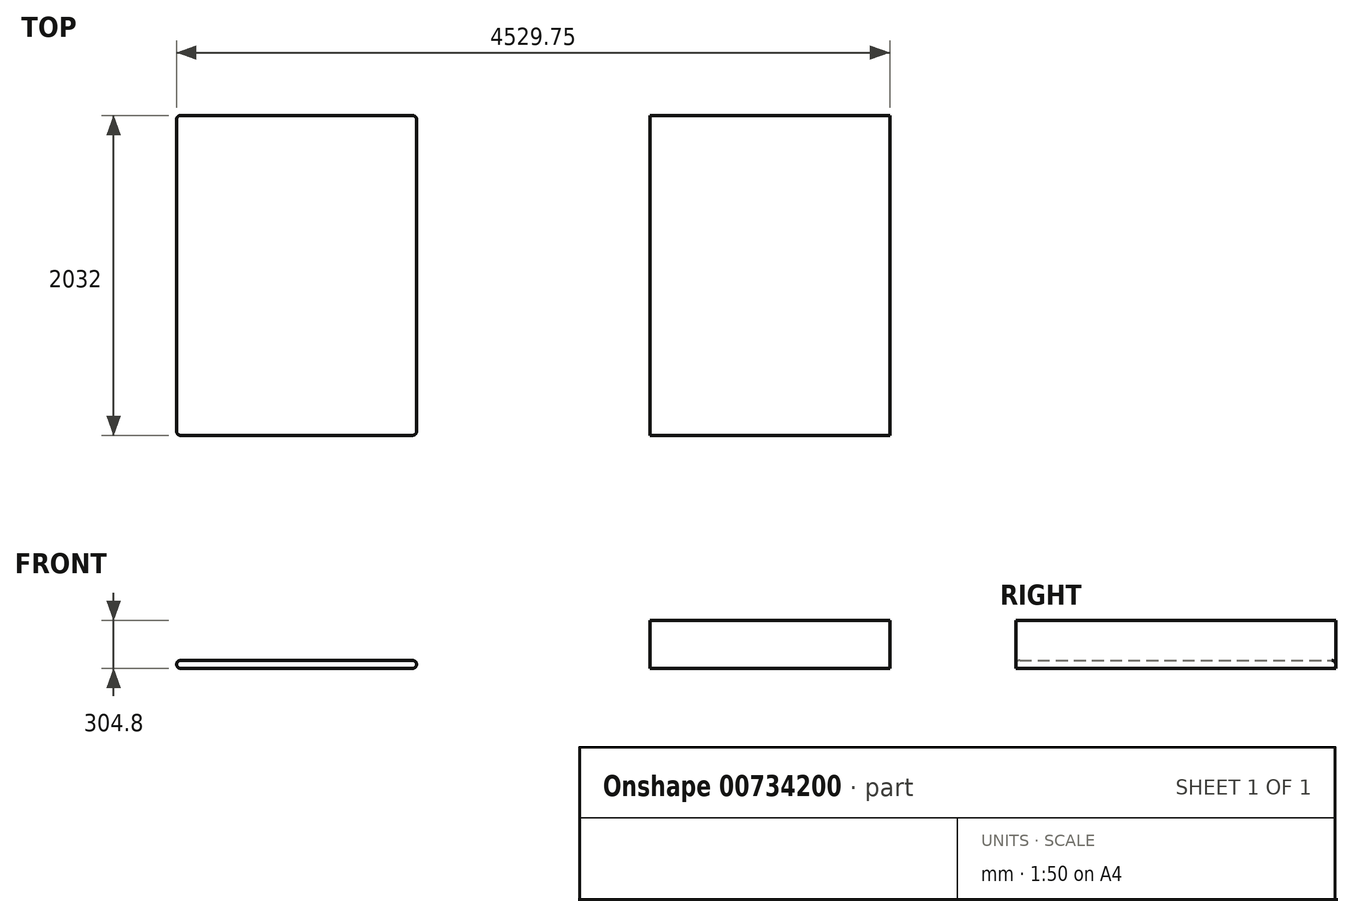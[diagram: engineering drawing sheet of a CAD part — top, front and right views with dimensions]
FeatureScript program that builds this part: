
annotation { "Feature Type Name" : "Feature", "Feature Type Description" : "" }
export const myFeature = defineFeature(function(context is Context, id is Id, definition is map)
    precondition{}
    {
        {
            var Q0;
            Q0=qCreatedBy(makeId("Top.planeOp"),FACE);
            var sketch = newSketch(context, id + "F0", { "sketchPlane" : qUnion([Q0])});
            skLineSegment(sketch, "E0.bottom", {"start": v(762, -1016) * mm, "end": v(-762, -1016) * mm});
            skLineSegment(sketch, "E0.top", {"start": v(762, 1016) * mm, "end": v(-762, 1016) * mm});
            skLineSegment(sketch, "E0.left", {"start": v(762, -1016) * mm, "end": v(762, 1016) * mm});
            skLineSegment(sketch, "E0.right", {"start": v(-762, -1016) * mm, "end": v(-762, 1016) * mm});
            skPoint(sketch, "E0.middle", {"position": v(0, 0) * mm});
            skSolve(sketch);
        }
        {
            var Q0;
            Q0=makeQuery(id+"F0.imprint","IMPRINT",FACE,{"disambiguationData":[TD([[makeQuery(id+"F0.imprint","IMPRINT",EDGE,{"derivedFrom":sQuery(id+"F0.wireOp",EDGE,"E0.bottom")}),-1.0]])]});
            extrude(context, id + "F1", {"entities" : qUnion([Q0]), "depth" : 304.8 * mm, "offsetDistance" : 25.4 * mm});
        }
        {
            var Q0;
            Q0=qCreatedBy(makeId("Top.planeOp"),FACE);
            var sketch = newSketch(context, id + "F2", { "sketchPlane" : qUnion([Q0])});
            skLineSegment(sketch, "E1.bottom", {"start": v(-2243.75, -1016) * mm, "end": v(-3767.75, -1016) * mm});
            skLineSegment(sketch, "E1.top", {"start": v(-2243.75, 1016) * mm, "end": v(-3767.75, 1016) * mm});
            skLineSegment(sketch, "E1.left", {"start": v(-2243.75, -1016) * mm, "end": v(-2243.75, 1016) * mm});
            skLineSegment(sketch, "E1.right", {"start": v(-3767.75, -1016) * mm, "end": v(-3767.75, 1016) * mm});
            skPoint(sketch, "E1.middle", {"position": v(-3005.75, 0) * mm});
            skSolve(sketch);
        }
        {
            var Q0;
            Q0=makeQuery(id+"F2.imprint","IMPRINT",FACE,{"disambiguationData":[TD([[makeQuery(id+"F2.imprint","IMPRINT",EDGE,{"derivedFrom":sQuery(id+"F2.wireOp",EDGE,"E1.bottom")}),-1.0]])]});
            extrude(context, id + "F3", {"entities" : qUnion([Q0]), "depth" : 50.8 * mm, "offsetDistance" : 25.4 * mm});
        }
        {
            var Q0;
            Q0=makeQuery(id+"F3.opExtrude","CAP_EDGE",EDGE,{"disambiguationData":[OSD([sQuery(id+"F2.wireOp",EDGE,"E1.left")])],"isStart":false});
            var Q1;
            Q1=makeQuery(id+"F3.opExtrude","CAP_EDGE",EDGE,{"disambiguationData":[OSD([sQuery(id+"F2.wireOp",EDGE,"E1.left")])],"isStart":true});
            var Q2;
            Q2=makeQuery(id+"F3.opExtrude","SWEPT_EDGE",EDGE,{"disambiguationData":[OSD([sQuery(id+"F2.wireOp",EDGE,"E1.bottom"),sQuery(id+"F2.wireOp",EDGE,"E1.left")])]});
            var Q3;
            Q3=makeQuery(id+"F3.opExtrude","CAP_EDGE",EDGE,{"disambiguationData":[OSD([sQuery(id+"F2.wireOp",EDGE,"E1.bottom")])],"isStart":false});
            var Q4;
            Q4=makeQuery(id+"F3.opExtrude","CAP_EDGE",EDGE,{"disambiguationData":[OSD([sQuery(id+"F2.wireOp",EDGE,"E1.right")])],"isStart":false});
            var Q5;
            Q5=makeQuery(id+"F3.opExtrude","SWEPT_EDGE",EDGE,{"disambiguationData":[OSD([sQuery(id+"F2.wireOp",EDGE,"E1.bottom"),sQuery(id+"F2.wireOp",EDGE,"E1.right")])]});
            var Q6;
            Q6=makeQuery(id+"F3.opExtrude","CAP_EDGE",EDGE,{"disambiguationData":[OSD([sQuery(id+"F2.wireOp",EDGE,"E1.bottom")])],"isStart":true});
            var Q7;
            Q7=makeQuery(id+"F3.opExtrude","CAP_EDGE",EDGE,{"disambiguationData":[OSD([sQuery(id+"F2.wireOp",EDGE,"E1.right")])],"isStart":true});
            var Q8;
            Q8=makeQuery(id+"F3.opExtrude","SWEPT_EDGE",EDGE,{"disambiguationData":[OSD([sQuery(id+"F2.wireOp",EDGE,"E1.top"),sQuery(id+"F2.wireOp",EDGE,"E1.right")])]});
            var Q9;
            Q9=makeQuery(id+"F3.opExtrude","CAP_EDGE",EDGE,{"disambiguationData":[OSD([sQuery(id+"F2.wireOp",EDGE,"E1.top")])],"isStart":true});
            var Q10;
            Q10=makeQuery(id+"F3.opExtrude","CAP_EDGE",EDGE,{"disambiguationData":[OSD([sQuery(id+"F2.wireOp",EDGE,"E1.top")])],"isStart":false});
            var Q11;
            Q11=makeQuery(id+"F3.opExtrude","SWEPT_EDGE",EDGE,{"disambiguationData":[OSD([sQuery(id+"F2.wireOp",EDGE,"E1.top"),sQuery(id+"F2.wireOp",EDGE,"E1.left")])]});
            fillet(context, id + "F4", {"entities" : qUnion([Q0, Q1, Q2, Q3, Q4, Q5, Q6, Q7, Q8, Q9, Q10, Q11]), "radius" : 25.4 * mm, "tangentPropagation" : true, "allowEdgeOverflow" : false});
        }
    });
